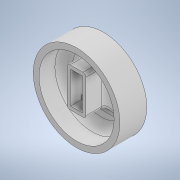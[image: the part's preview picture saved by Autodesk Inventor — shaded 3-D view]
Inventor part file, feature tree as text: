
AUTODESK INVENTOR PART (.ipt)
format: ipt  version: 2021 (Build 250183000, 183)  size: 287,232 bytes
history: native  units: mm
features: extrude x7, sketch x7, fillet x2
ambient origin geometry x8: Origin, YZ Plane, XZ Plane, XY Plane, X Axis, Y Axis, Z Axis, Center Point
bodies: Solid1 (feature_tree)
feature tree (16):
  extrude  "Extrusion1"  Depth=46.5mm TaperAngle=0.0deg
  extrude  "Extrusion2"  Depth=40.5mm
  extrude  "Extrusion3"  Depth=10.25mm
  extrude  "Extrusion4"  Depth=5.0mm
  extrude  "Extrusion5"  Depth=5.0mm
  fillet  "Fillet1"  Radius=46.5mm
  fillet  "Fillet2"  Radius=5.0mm
  extrude  "Extrusion6"  Depth=2.5mm TaperAngle=0.0deg
  extrude  "Extrusion7"  Depth=10.0mm
  sketch  "Sketch1"  dims[d0=150.0mm d1=46.5mm d2=0.0mm]
  sketch  "Sketch2"  dims[d5=20.5mm d6=40.5mm]
  sketch  "Sketch4"  dims[d8=10.125mm d9=10.25mm]
  sketch  "Sketch5"  dims[d10=6.5mm d11=5.0mm]
  sketch  "Sketch6"  dims[d12=0.0mm d13=7.0mm d14=46.5mm d15=0.0mm d16=5.0mm]
  sketch  "Sketch7"  dims[d17=0.75mm d18=2.5mm d19=0.0mm]
  sketch  "Sketch8"  dims[d20=55.5mm d21=7.5mm d22=19.0mm d23=0.0mm d24=10.0mm d25=6.0mm d26=42.5mm d27=0.0mm d28=15.0mm d29=5.0mm d30=135.0deg d31=4.0mm d32=40.0mm d34=360.0deg d36=41.5mm d37=20.75mm d38=0.0mm d39=0.0mm d40=10.0mm d41=40.0mm d43=360.0deg d45=41.5mm d46=0.0mm]
